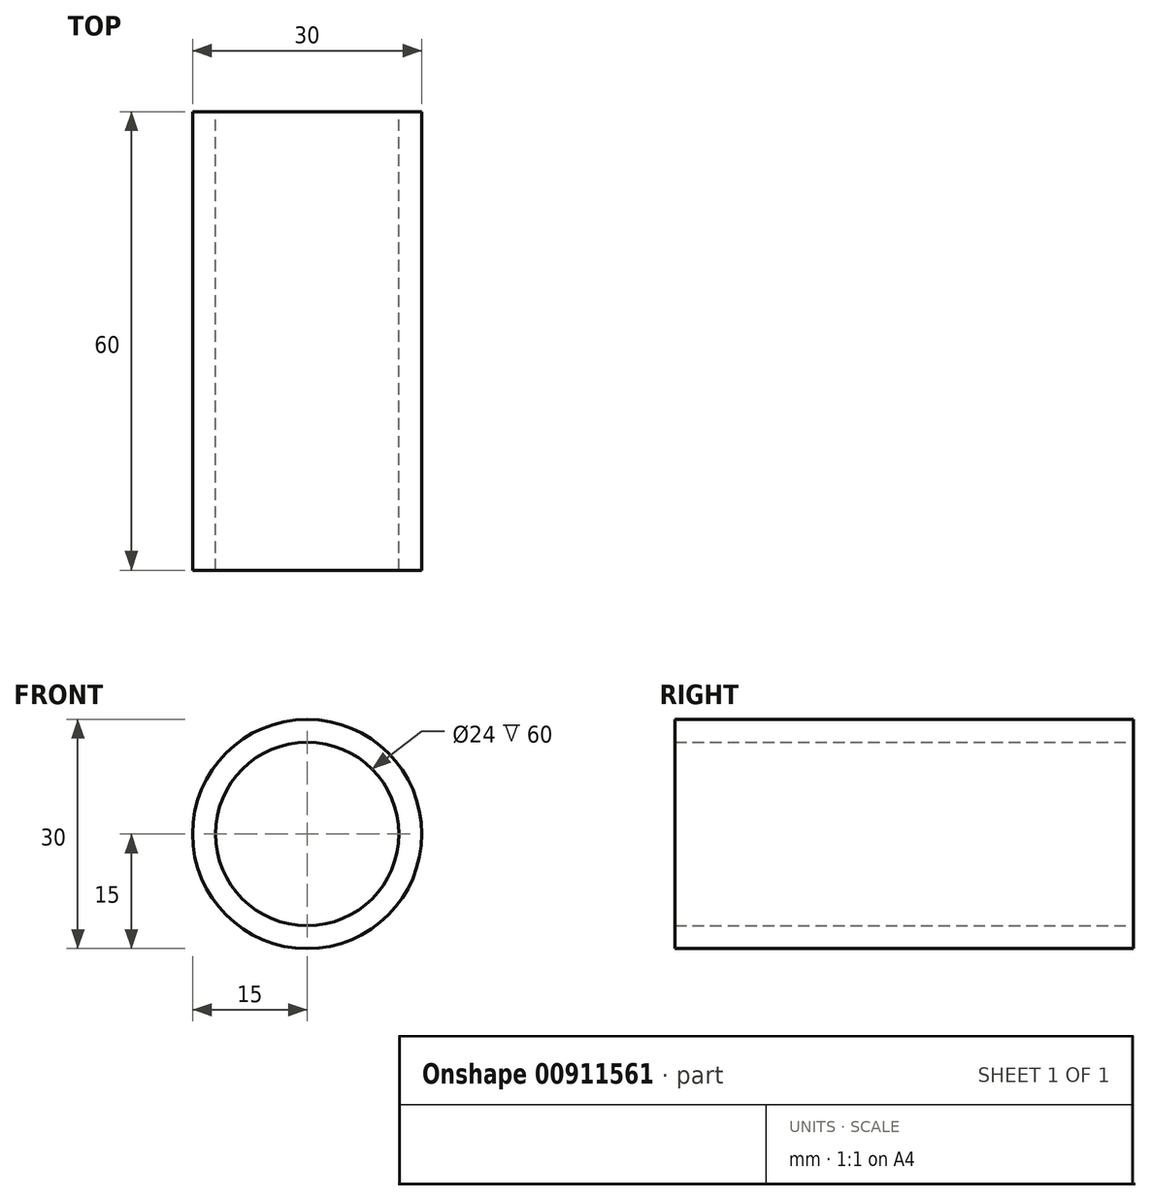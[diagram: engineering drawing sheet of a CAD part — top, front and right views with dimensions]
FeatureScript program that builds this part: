
annotation { "Feature Type Name" : "Feature", "Feature Type Description" : "" }
export const myFeature = defineFeature(function(context is Context, id is Id, definition is map)
    precondition{}
    {
        {
            var Q0;
            Q0=qCreatedBy(makeId("Front.planeOp"),FACE);
            var sketch = newSketch(context, id + "F0", { "sketchPlane" : qUnion([Q0])});
            skCircle(sketch, "E0", {"center": v(0, 0) * mm, "radius": 12 * mm});
            skCircle(sketch, "E1", {"center": v(0, 0) * mm, "radius": 15 * mm});
            skSolve(sketch);
        }
        {
            var Q0;
            Q0=makeQuery(id+"F0.imprint","IMPRINT",FACE,{"disambiguationData":[TD([[makeQuery(id+"F0.imprint","IMPRINT",EDGE,{"derivedFrom":sQuery(id+"F0.wireOp",EDGE,"E0")}),-1.0]])]});
            extrude(context, id + "F1", {"entities" : qUnion([Q0]), "depth" : 60 * mm, "offsetDistance" : 25 * mm});
        }
    });
